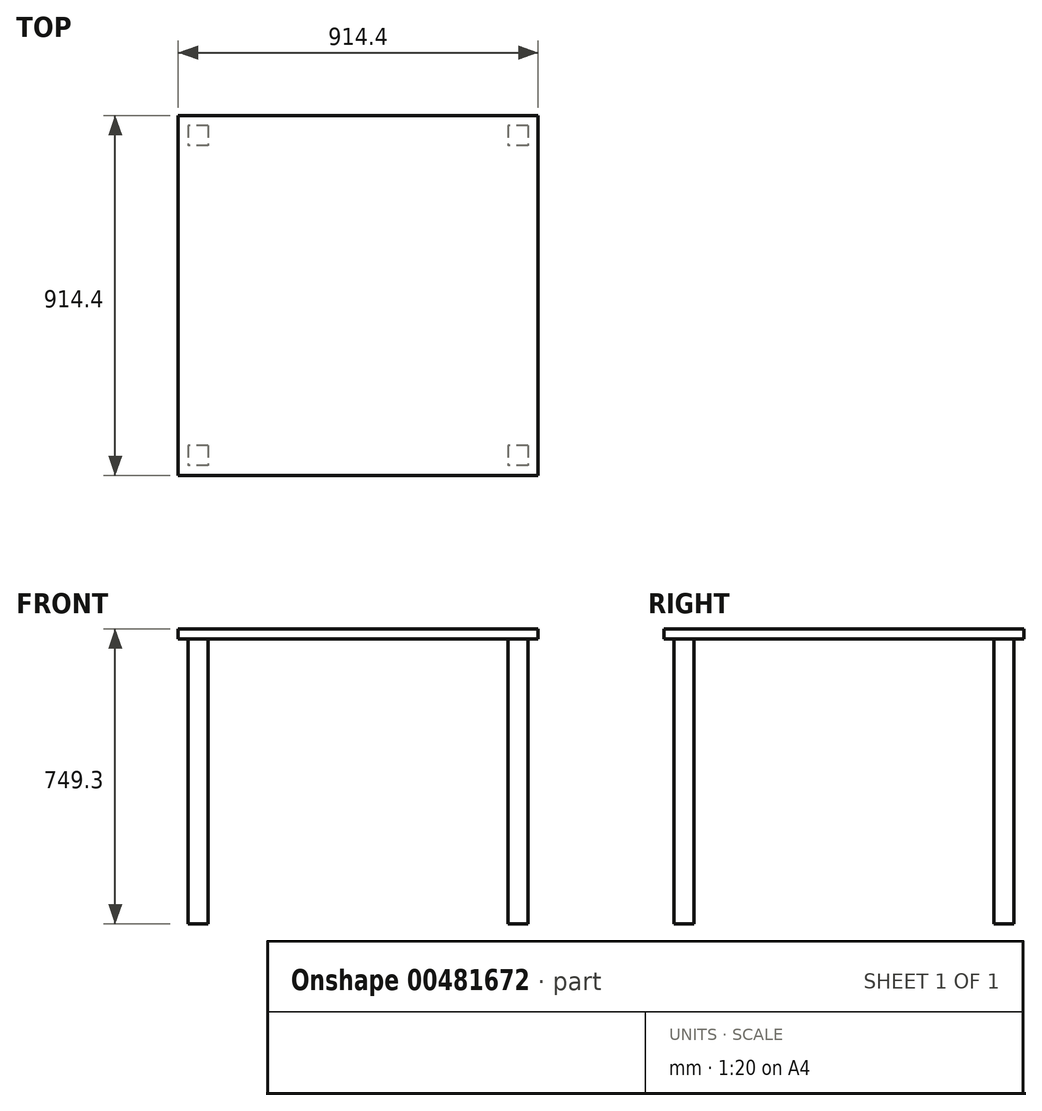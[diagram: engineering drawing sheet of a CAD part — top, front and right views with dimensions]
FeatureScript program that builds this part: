
annotation { "Feature Type Name" : "Feature", "Feature Type Description" : "" }
export const myFeature = defineFeature(function(context is Context, id is Id, definition is map)
    precondition{}
    {
        {
            var Q0;
            Q0=qCreatedBy(makeId("Top.planeOp"),FACE);
            var sketch = newSketch(context, id + "F0", { "sketchPlane" : qUnion([Q0])});
            skLineSegment(sketch, "E0.bottom", {"start": v(457.2, 457.2) * mm, "end": v(-457.2, 457.2) * mm});
            skLineSegment(sketch, "E0.top", {"start": v(457.2, -457.2) * mm, "end": v(-457.2, -457.2) * mm});
            skLineSegment(sketch, "E0.left", {"start": v(457.2, 457.2) * mm, "end": v(457.2, -457.2) * mm});
            skLineSegment(sketch, "E0.right", {"start": v(-457.2, 457.2) * mm, "end": v(-457.2, -457.2) * mm});
            skPoint(sketch, "E0.middle", {"position": v(0, 0) * mm});
            skSolve(sketch);
        }
        {
            var Q0;
            Q0=makeQuery(id+"F0.imprint","IMPRINT",FACE,{"disambiguationData":[TD([[makeQuery(id+"F0.imprint","IMPRINT",EDGE,{"derivedFrom":sQuery(id+"F0.wireOp",EDGE,"E0.bottom")}),1.0]])]});
            extrude(context, id + "F1", {"entities" : qUnion([Q0]), "depth" : 25.4 * mm});
        }
        {
            var Q0;
            Q0=makeQuery(id+"F1.opExtrude","CAP_FACE",FACE,{"disambiguationData":[OSD([sQuery(id+"F0.wireOp",EDGE,"E0.bottom"),sQuery(id+"F0.wireOp",EDGE,"E0.top"),sQuery(id+"F0.wireOp",EDGE,"E0.left"),sQuery(id+"F0.wireOp",EDGE,"E0.right")])],"isStart":true});
            var sketch = newSketch(context, id + "F2", { "sketchPlane" : qUnion([Q0])});
            skLineSegment(sketch, "E1.bottom", {"start": v(-381, 381) * mm, "end": v(-431.8, 381) * mm});
            skLineSegment(sketch, "E1.top", {"start": v(-381, 431.8) * mm, "end": v(-431.8, 431.8) * mm});
            skLineSegment(sketch, "E1.left", {"start": v(-381, 381) * mm, "end": v(-381, 431.8) * mm});
            skLineSegment(sketch, "E1.right", {"start": v(-431.8, 381) * mm, "end": v(-431.8, 431.8) * mm});
            skPoint(sketch, "E1.middle", {"position": v(-406.4, 406.4) * mm});
            skLineSegment(sketch, "E2.0.1.0", {"start": v(-431.8, -431.8) * mm, "end": v(-431.8, -381) * mm});
            skLineSegment(sketch, "E2.0.1.1", {"start": v(-381, -431.8) * mm, "end": v(-381, -381) * mm});
            skLineSegment(sketch, "E2.0.1.2", {"start": v(-381, -381) * mm, "end": v(-431.8, -381) * mm});
            skLineSegment(sketch, "E2.0.1.3", {"start": v(-381, -431.8) * mm, "end": v(-431.8, -431.8) * mm});
            skPoint(sketch, "E2.0.1.4", {"position": v(-406.4, -406.4) * mm});
            skLineSegment(sketch, "E2.1.0.0", {"start": v(381, 381) * mm, "end": v(381, 431.8) * mm});
            skLineSegment(sketch, "E2.1.0.1", {"start": v(431.8, 381) * mm, "end": v(431.8, 431.8) * mm});
            skLineSegment(sketch, "E2.1.0.2", {"start": v(431.8, 431.8) * mm, "end": v(381, 431.8) * mm});
            skLineSegment(sketch, "E2.1.0.3", {"start": v(431.8, 381) * mm, "end": v(381, 381) * mm});
            skPoint(sketch, "E2.1.0.4", {"position": v(406.4, 406.4) * mm});
            skLineSegment(sketch, "E2.1.1.0", {"start": v(381, -431.8) * mm, "end": v(381, -381) * mm});
            skLineSegment(sketch, "E2.1.1.1", {"start": v(431.8, -431.8) * mm, "end": v(431.8, -381) * mm});
            skLineSegment(sketch, "E2.1.1.2", {"start": v(431.8, -381) * mm, "end": v(381, -381) * mm});
            skLineSegment(sketch, "E2.1.1.3", {"start": v(431.8, -431.8) * mm, "end": v(381, -431.8) * mm});
            skPoint(sketch, "E2.1.1.4", {"position": v(406.4, -406.4) * mm});
            skLineSegment(sketch, "E2.direction1", {"start": v(-431.8, 381) * mm, "end": v(381, 381) * mm, "construction": true});
            skLineSegment(sketch, "E2.direction2", {"start": v(-431.8, 381) * mm, "end": v(-431.8, -431.8) * mm, "construction": true});
            skSolve(sketch);
        }
        {
            var Q0;
            Q0=qSketchRegion(id+"F2",true);
            extrude(context, id + "F3", {"entities" : qUnion([Q0]), "operationType" : NewBodyOperationType.ADD, "depth" : 723.9 * mm});
        }
    });
